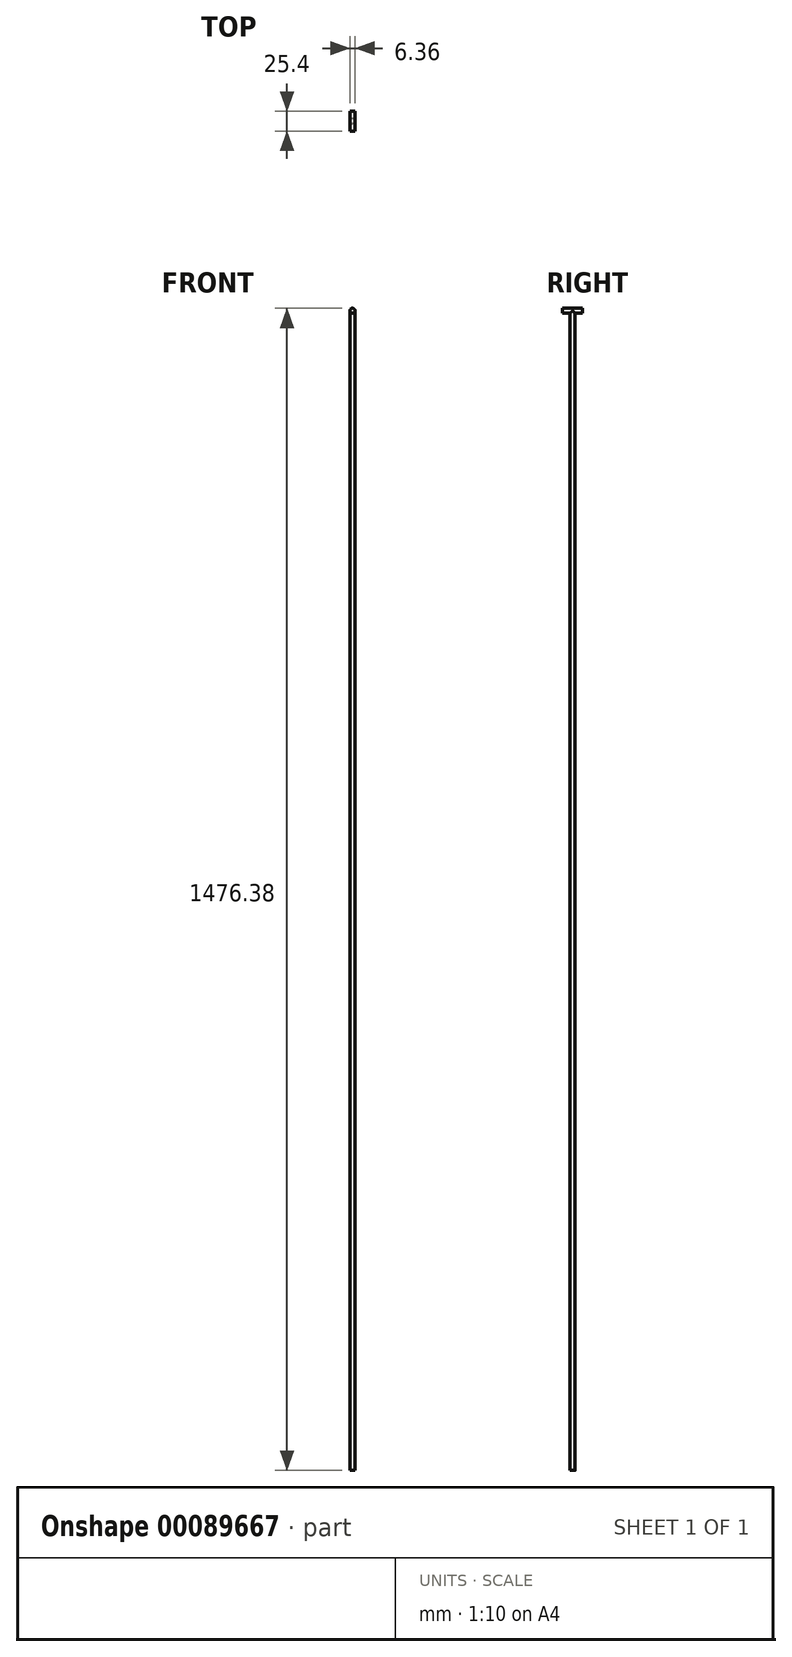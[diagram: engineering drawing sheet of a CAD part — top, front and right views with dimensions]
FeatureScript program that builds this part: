
annotation { "Feature Type Name" : "Feature", "Feature Type Description" : "" }
export const myFeature = defineFeature(function(context is Context, id is Id, definition is map)
    precondition{}
    {
        {
            var Q0;
            Q0=qCreatedBy(makeId("Front.planeOp"),FACE);
            var sketch = newSketch(context, id + "F0", { "sketchPlane" : qUnion([Q0])});
            skLineSegment(sketch, "E0.bottom", {"start": v(-3.18, 736.6) * mm, "end": v(3.17, 736.6) * mm});
            skLineSegment(sketch, "E0.top", {"start": v(-3.17, -736.6) * mm, "end": v(3.18, -736.6) * mm});
            skLineSegment(sketch, "E0.left", {"start": v(-3.18, 736.6) * mm, "end": v(-3.17, -736.6) * mm});
            skLineSegment(sketch, "E0.right", {"start": v(3.17, 736.6) * mm, "end": v(3.18, -736.6) * mm});
            skPoint(sketch, "E0.middle", {"position": v(0, 0) * mm});
            skLineSegment(sketch, "E1.top", {"start": v(-3.18, 730.25) * mm, "end": v(3.17, 730.25) * mm});
            skLineSegment(sketch, "E1.left", {"start": v(-3.18, 736.6) * mm, "end": v(-3.18, 730.25) * mm});
            skLineSegment(sketch, "E1.right", {"start": v(3.17, 736.6) * mm, "end": v(3.17, 730.25) * mm});
            skSolve(sketch);
        }
        {
            var Q0;
            Q0=makeQuery(id+"F0.imprint","IMPRINT",FACE,{"disambiguationData":[TD([[makeQuery(id+"F0.imprint","IMPRINT",EDGE,{"derivedFrom":sQuery(id+"F0.wireOp",EDGE,"E0.bottom")}),-1.0]])]});
            var Q1;
            Q1=makeQuery(id+"F0.imprint","IMPRINT",FACE,{"disambiguationData":[TD([[makeQuery(id+"F0.imprint","IMPRINT",EDGE,{"derivedFrom":sQuery(id+"F0.wireOp",EDGE,"E0.top")}),1.0]])]});
            extrude(context, id + "F1", {"entities" : qUnion([Q0, Q1]), "endBound" : BoundingType.SYMMETRIC, "depth" : 6.35 * mm});
        }
        {
            var Q0;
            Q0=qCreatedBy(makeId("Front.planeOp"),FACE);
            var sketch = newSketch(context, id + "F2", { "sketchPlane" : qUnion([Q0])});
            skCircle(sketch, "E2", {"center": v(0, 736.6) * mm, "radius": 3.18 * mm});
            skSolve(sketch);
        }
        {
            var Q0;
            Q0 = qSketchRegion(id + "F2", true);
            extrude(context, id + "F3", {"entities" : qUnion([Q0]), "operationType" : NewBodyOperationType.ADD, "endBound" : BoundingType.SYMMETRIC, "depth" : 25.4 * mm});
        }
        {
            var Q0;
            Q0=makeQuery(id+"F1.opExtrude","CAP_EDGE",EDGE,{"disambiguationData":[OSD([sQuery(id+"F0.wireOp",EDGE,"E0.right"),sQuery(id+"F0.wireOp",EDGE,"E1.right")])],"isStart":false});
            var Q1;
            Q1=makeQuery(id+"F1.opExtrude","CAP_EDGE",EDGE,{"disambiguationData":[OSD([sQuery(id+"F0.wireOp",EDGE,"E0.right"),sQuery(id+"F0.wireOp",EDGE,"E1.right")])],"isStart":true});
            var Q2;
            Q2=makeQuery(id+"F1.opExtrude","CAP_EDGE",EDGE,{"disambiguationData":[OSD([sQuery(id+"F0.wireOp",EDGE,"E0.left"),sQuery(id+"F0.wireOp",EDGE,"E1.left")])],"isStart":true});
            var Q3;
            Q3=makeQuery(id+"F1.opExtrude","CAP_EDGE",EDGE,{"disambiguationData":[OSD([sQuery(id+"F0.wireOp",EDGE,"E0.left"),sQuery(id+"F0.wireOp",EDGE,"E1.left")])],"isStart":false});
            fillet(context, id + "F4", {"entities" : qUnion([Q0, Q1, Q2, Q3]), "radius" : 3.17 * mm, "tangentPropagation" : true, "allowEdgeOverflow" : false});
        }
    });
